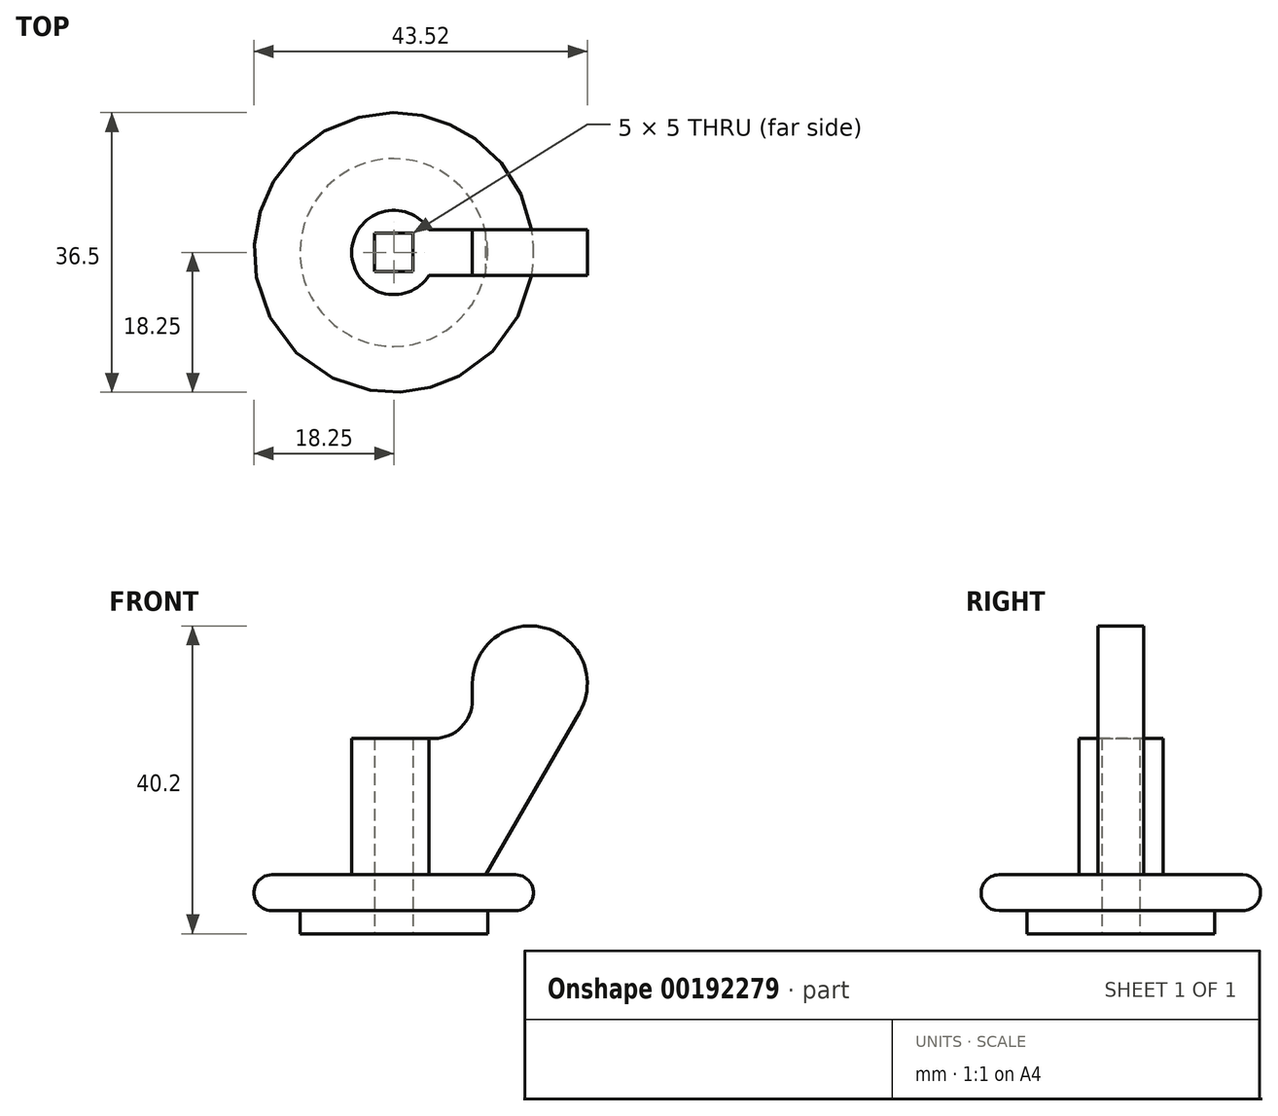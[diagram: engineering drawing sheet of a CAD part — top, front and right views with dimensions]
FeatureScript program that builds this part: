
annotation { "Feature Type Name" : "Feature", "Feature Type Description" : "" }
export const myFeature = defineFeature(function(context is Context, id is Id, definition is map)
    precondition{}
    {
        {
            var Q0;
            Q0=qCreatedBy(makeId("Front.planeOp"),FACE);
            var sketch = newSketch(context, id + "F0", { "sketchPlane" : qUnion([Q0])});
            skLineSegment(sketch, "E0", {"start": v(0, 0) * mm, "end": v(0, -12) * mm, "construction": true});
            skLineSegment(sketch, "E1", {"start": v(0, 0) * mm, "end": v(15.9, 0) * mm});
            skLineSegment(sketch, "E2", {"start": v(15.9, 0) * mm, "end": v(15.9, -4.7) * mm, "construction": true});
            skLineSegment(sketch, "E3", {"start": v(15.9, -4.7) * mm, "end": v(12.25, -4.7) * mm});
            skLineSegment(sketch, "E4", {"start": v(12.25, -4.7) * mm, "end": v(12.25, -7.7) * mm});
            skLineSegment(sketch, "E5", {"start": v(12.25, -7.7) * mm, "end": v(0, -7.7) * mm});
            skLineSegment(sketch, "E6", {"start": v(0, -7.7) * mm, "end": v(0, 0) * mm});
            skArc(sketch, "E7", {"start": v(15.9, -4.7) * mm, "mid": v(18.25, -2.35) * mm, "end": v(15.9, 0) * mm});
            skSolve(sketch);
        }
        {
            var Q0;
            Q0=makeQuery(id+"F0.imprint","IMPRINT",FACE,{"disambiguationData":[TD([[makeQuery(id+"F0.imprint","IMPRINT",EDGE,{"derivedFrom":sQuery(id+"F0.wireOp",EDGE,"E1")}),-1.0]])]});
            var Q1;
            Q1=sQuery(id+"F0.wireOp",EDGE,"E0");
            revolve(context, id + "F1", {"entities" : qUnion([Q0]), "axis" : qUnion([Q1]), "revolveType" : RevolveType.FULL});
        }
        {
            var Q0;
            Q0=qCreatedBy(makeId("Front.planeOp"),FACE);
            var sketch = newSketch(context, id + "F2", { "sketchPlane" : qUnion([Q0])});
            skLineSegment(sketch, "E8", {"start": v(0, -14.74) * mm, "end": v(0, 0) * mm, "construction": true});
            skLineSegment(sketch, "E9", {"start": v(0, 0) * mm, "end": v(12, 0) * mm});
            skLineSegment(sketch, "E10", {"start": v(12, 0) * mm, "end": v(24.27, 21.25) * mm});
            skLineSegment(sketch, "E11", {"start": v(0, 0) * mm, "end": v(0, 17.8) * mm});
            skLineSegment(sketch, "E12", {"start": v(0, 17.8) * mm, "end": v(5.27, 17.8) * mm});
            skLineSegment(sketch, "E13", {"start": v(5.5, 30.97) * mm, "end": v(5.5, 18.55) * mm, "construction": true});
            skArc(sketch, "E14", {"start": v(24.27, 21.25) * mm, "mid": v(19.71, 32.24) * mm, "end": v(10.27, 25) * mm});
            skLineSegment(sketch, "E15", {"start": v(10.27, 22.8) * mm, "end": v(10.27, 25) * mm});
            skPoint(sketch, "E16.visualSharp", {"position": v(10.27, 17.8) * mm});
            skArc(sketch, "E16.filletArc", {"start": v(5.27, 17.8) * mm, "mid": v(8.8, 19.26) * mm, "end": v(10.27, 22.8) * mm});
            skSolve(sketch);
        }
        {
            var Q0;
            Q0=makeQuery(id+"F2.imprint","IMPRINT",FACE,{"disambiguationData":[TD([[makeQuery(id+"F2.imprint","IMPRINT",EDGE,{"derivedFrom":sQuery(id+"F2.wireOp",EDGE,"woGXxxkb-9tDG-oYuA-yCW7-UuS0mcRSNjpq")}),1.0]])]});
            var Q1;
            Q1=makeQuery(id+"F2.imprint","IMPRINT",FACE,{"disambiguationData":[TD([[makeQuery(id+"F2.imprint","IMPRINT",EDGE,{"derivedFrom":sQuery(id+"F2.wireOp",EDGE,"E9")}),1.0]])]});
            extrude(context, id + "F3", {"entities" : qUnion([Q0, Q1]), "operationType" : NewBodyOperationType.ADD, "depth" : 3 * mm, "offsetDistance" : 25 * mm, "hasSecondDirection" : true, "secondDirectionOppositeDirection" : true, "secondDirectionDepth" : 3 * mm});
        }
        {
            var Q0;
            Q0=makeQuery(id+"F1.opRevolve","SWEPT_FACE",FACE,{"disambiguationData":[OSD([sQuery(id+"F0.wireOp",EDGE,"E5")])]});
            var sketch = newSketch(context, id + "F4", { "sketchPlane" : qUnion([Q0])});
            skCircle(sketch, "E17", {"center": v(0, 0) * mm, "radius": 5.5 * mm});
            skLineSegment(sketch, "E18.bottom", {"start": v(2.5, -2.5) * mm, "end": v(-2.5, -2.5) * mm});
            skLineSegment(sketch, "E18.top", {"start": v(2.5, 2.5) * mm, "end": v(-2.5, 2.5) * mm});
            skLineSegment(sketch, "E18.left", {"start": v(2.5, -2.5) * mm, "end": v(2.5, 2.5) * mm});
            skLineSegment(sketch, "E18.right", {"start": v(-2.5, -2.5) * mm, "end": v(-2.5, 2.5) * mm});
            skSolve(sketch);
        }
        {
            var Q0;
            Q0=makeQuery(id+"F4.imprint","IMPRINT",FACE,{"disambiguationData":[TD([[makeQuery(id+"F4.imprint","IMPRINT",EDGE,{"derivedFrom":sQuery(id+"F4.wireOp",EDGE,"E17")}),1.0]])]});
            var Q1;
            {var subQ0=sQuery(id+"F2.wireOp",EDGE,"E12");Q1=makeQuery(id+"FrppzYYOcWl1lQH_1.1.F3.boolean.opBoolean","MERGE",FACE,{"derivedFrom":[makeQuery(id+"F3.opExtrude","SWEPT_FACE",FACE,{"disambiguationData":[OSD([subQ0])]}),makeQuery(id+"FrppzYYOcWl1lQH_1.1.F3.opExtrude","SWEPT_FACE",FACE,{"disambiguationData":[OSD([subQ0])]})]});}
            extrude(context, id + "F5", {"entities" : qUnion([Q0]), "operationType" : NewBodyOperationType.ADD, "endBound" : BoundingType.UP_TO_SURFACE, "oppositeDirection" : true, "depth" : 25.5 * mm, "endBoundEntityFace" : qUnion([Q1]), "offsetDistance" : 25 * mm});
        }
        {
            var Q0;
            Q0=makeQuery(id+"F4.imprint","IMPRINT",FACE,{"disambiguationData":[TD([[makeQuery(id+"F4.imprint","IMPRINT",EDGE,{"derivedFrom":sQuery(id+"F4.wireOp",EDGE,"E18.bottom")}),-1.0]])]});
            extrude(context, id + "F6", {"entities" : qUnion([Q0]), "operationType" : NewBodyOperationType.REMOVE, "endBound" : BoundingType.THROUGH_ALL, "oppositeDirection" : true, "depth" : 25 * mm, "offsetDistance" : 25 * mm});
        }
    });
